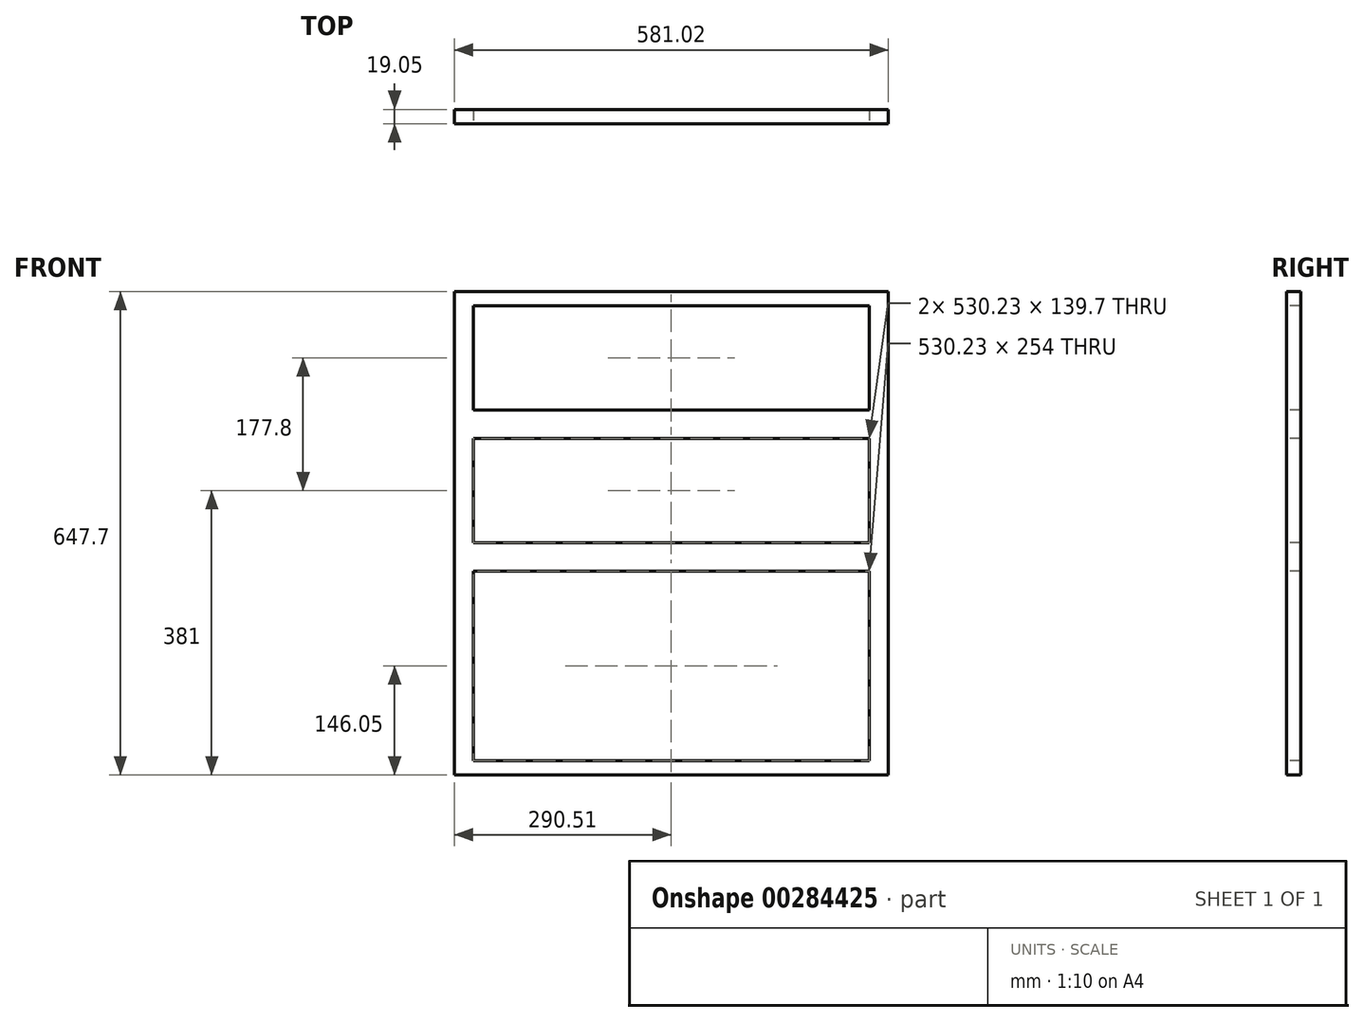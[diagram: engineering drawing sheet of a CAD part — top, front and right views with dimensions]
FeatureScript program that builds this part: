
annotation { "Feature Type Name" : "Feature", "Feature Type Description" : "" }
export const myFeature = defineFeature(function(context is Context, id is Id, definition is map)
    precondition{}
    {
        {
            var Q0;
            Q0=qCreatedBy(makeId("Front.planeOp"),FACE);
            var sketch = newSketch(context, id + "F0", { "sketchPlane" : qUnion([Q0])});
            skLineSegment(sketch, "E0.bottom", {"start": v(290.51, 0) * mm, "end": v(-290.51, 0) * mm});
            skLineSegment(sketch, "E0.top", {"start": v(290.51, 647.7) * mm, "end": v(-290.51, 647.7) * mm});
            skLineSegment(sketch, "E0.left", {"start": v(290.51, 0) * mm, "end": v(290.51, 647.7) * mm});
            skLineSegment(sketch, "E0.right", {"start": v(-290.51, 0) * mm, "end": v(-290.51, 647.7) * mm});
            skPoint(sketch, "E0.middle", {"position": v(0, 323.85) * mm});
            skLineSegment(sketch, "E1.bottom", {"start": v(265.11, 628.65) * mm, "end": v(-265.11, 628.65) * mm});
            skLineSegment(sketch, "E1.top", {"start": v(265.11, 488.95) * mm, "end": v(-265.11, 488.95) * mm});
            skLineSegment(sketch, "E1.left", {"start": v(265.11, 628.65) * mm, "end": v(265.11, 488.95) * mm});
            skLineSegment(sketch, "E1.right", {"start": v(-265.11, 628.65) * mm, "end": v(-265.11, 488.95) * mm});
            skPoint(sketch, "E1.middle", {"position": v(0, 558.8) * mm});
            skLineSegment(sketch, "E2.bottom", {"start": v(265.11, 450.85) * mm, "end": v(-265.11, 450.85) * mm});
            skLineSegment(sketch, "E2.top", {"start": v(265.11, 311.15) * mm, "end": v(-265.11, 311.15) * mm});
            skLineSegment(sketch, "E2.left", {"start": v(265.11, 450.85) * mm, "end": v(265.11, 311.15) * mm});
            skLineSegment(sketch, "E2.right", {"start": v(-265.11, 450.85) * mm, "end": v(-265.11, 311.15) * mm});
            skPoint(sketch, "E2.middle", {"position": v(0, 381) * mm});
            skLineSegment(sketch, "E3.bottom", {"start": v(265.11, 273.05) * mm, "end": v(-265.11, 273.05) * mm});
            skLineSegment(sketch, "E3.top", {"start": v(265.11, 19.05) * mm, "end": v(-265.11, 19.05) * mm});
            skLineSegment(sketch, "E3.left", {"start": v(265.11, 273.05) * mm, "end": v(265.11, 19.05) * mm});
            skLineSegment(sketch, "E3.right", {"start": v(-265.11, 273.05) * mm, "end": v(-265.11, 19.05) * mm});
            skPoint(sketch, "E3.middle", {"position": v(0, 146.05) * mm});
            skSolve(sketch);
        }
        {
            var Q0;
            Q0=makeQuery(id+"F0.imprint","IMPRINT",FACE,{"disambiguationData":[TD([[makeQuery(id+"F0.imprint","IMPRINT",EDGE,{"derivedFrom":sQuery(id+"F0.wireOp",EDGE,"E0.bottom")}),-1.0]])]});
            extrude(context, id + "F1", {"entities" : qUnion([Q0]), "oppositeDirection" : true, "depth" : 19.05 * mm});
        }
    });
